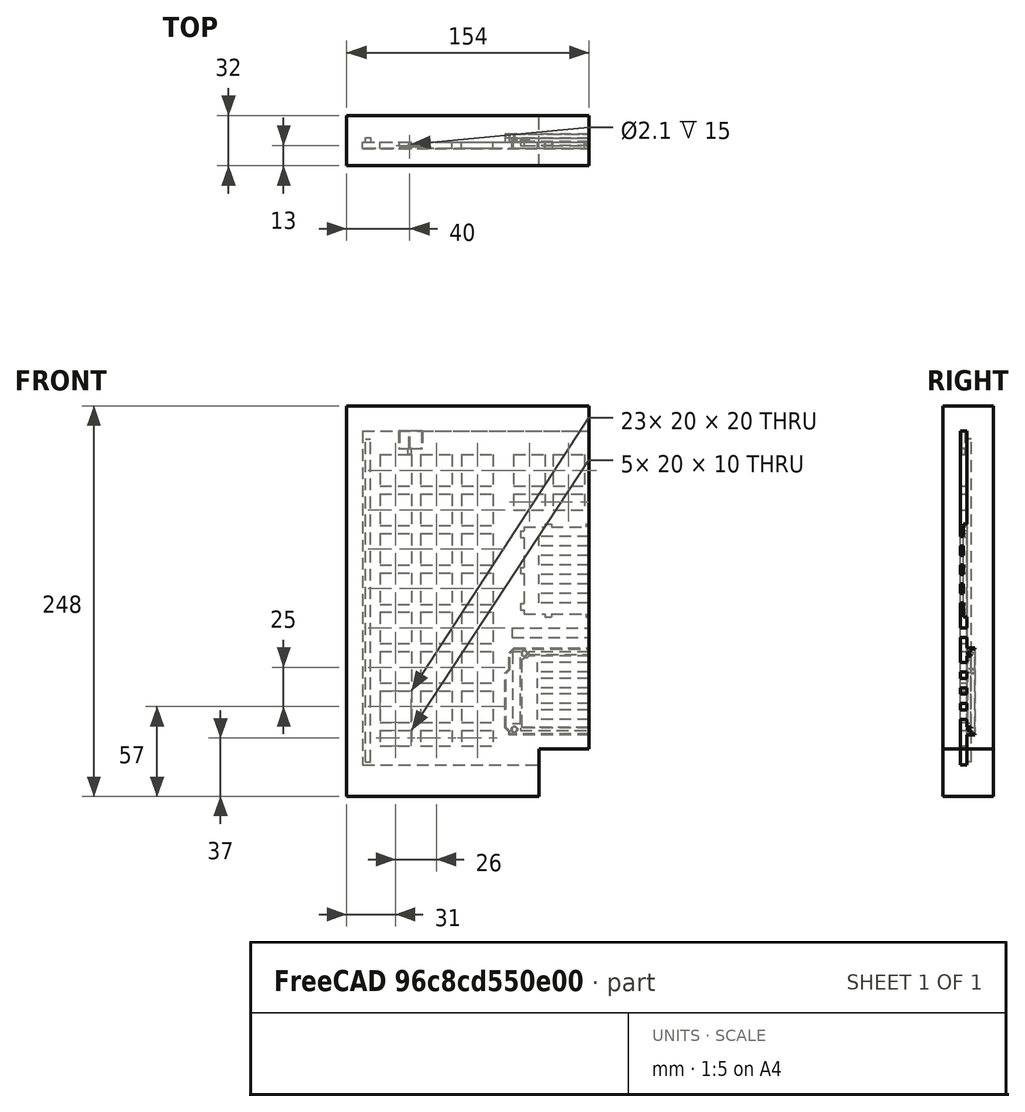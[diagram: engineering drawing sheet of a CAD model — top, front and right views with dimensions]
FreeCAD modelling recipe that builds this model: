
FCSTD DOCUMENT  (FreeCAD 0.17R13522 (Git))
Label: base_para_arduino_y_matrizia_izquierda
License: CreativeCommons Attribution-ShareAlike
LicenseURL: http://creativecommons.org/licenses/by-sa/4.0/
objects: Part::Box×18, Part::Cut×18, Part::Feature×11, Part::Fuse×9, Part::FeaturePython×6
note: 62 computed .brp shape members not serialized (recipe doc carries the construction recipe); baked Part::Feature solids carry a one-line shape summary decoded from their .brp

FEATURE [Part::Feature] Cut001001001002003001008002002034001  label="base de la base con agujeros"
  shape: bbox 280 x 4 x 200 mm, 10 faces (baked)
FEATURE [Part::Box] Box  label="fleje apoyo lateral izquierdo"
  AttacherType = Attacher::AttachEngine3D
  Height = 200
  Length = 3
  Placement = pos=(2,0,-308) rot=(0,0,1;0rad)
  Width = 3
FEATURE [Part::Feature] Box001  label="fleje apoyo lateral derecho"
  Placement = pos=(283,0,-308) rot=(0,0,1;0rad)
  shape: bbox 3 x 3 x 200 mm, 6 faces (baked)
FEATURE [Part::Box] Box002  label="Cube"
  AttacherType = Attacher::AttachEngine3D
  Height = 200
  Length = 8
  Placement = pos=(280,-4,-308) rot=(0,0,1;0rad)
  Width = 4
FEATURE [Part::Fuse] Fusion
  Base = -> Cut001001001002003001008002002034001
  Refine = true
  Tool = -> Box002
FEATURE [Part::Fuse] Fusion001
  Base = -> Box001
  Refine = true
  Tool = -> Fusion
FEATURE [Part::Fuse] Fusion002
  Base = -> Box
  Refine = true
  Tool = -> Fusion001
FEATURE [Part::Box] Box003  label="Cube001"
  AttacherType = Attacher::AttachEngine3D
  Height = 10
  Length = 10
  Placement = pos=(-2,0,-112) rot=(0,0,1;0rad)
  Width = 10
FEATURE [Part::Feature] Box003001  label="Cube002"
  Placement = pos=(280,0,-112) rot=(0,0,1;0rad)
  shape: bbox 10 x 10 x 10 mm, 6 faces (baked)
FEATURE [Part::Cut] Cut
  Base = -> Fusion002
  Refine = true
  Tool = -> Box003
FEATURE [Part::Cut] Cut001001001002003001008002002034002  label="base sin soportes y sin recorte horizontal"
  Base = -> Cut
  Refine = true
  Tool = -> Box003001
FEATURE [Part::Feature] Fusion011001  label="cortador matrizia001"
  Placement = pos=(102.5,1,-224) rot=(1,0,0;1.5708rad)
  shape: bbox 87 x 3 x 59 mm, 54 faces (baked)
FEATURE [Part::Cut] Cut001001001002003001008002002034003
  Base = -> Cut001001001002003001008002002034002
  Refine = true
  Tool = -> Fusion011001
FEATURE [Part::Box] Box003002  label="Cube003"
  AttacherType = Attacher::AttachEngine3D
  Height = 200
  Length = 288
  Placement = pos=(0,-4,-508) rot=(0,0,1;0rad)
  Width = 4
FEATURE [Part::Feature] Box003003  label="fleje apoyo lateral izquierdo001"
  Placement = pos=(2,0,-506) rot=(0,0,1;0rad)
  shape: bbox 3 x 3 x 200 mm, 6 faces (baked)
FEATURE [Part::Feature] Box001001  label="fleje apoyo lateral derecho001"
  Placement = pos=(283,0,-507) rot=(0,0,1;0rad)
  shape: bbox 3 x 3 x 200 mm, 6 faces (baked)
FEATURE [Part::Fuse] Fusion011002
  Base = -> Cut001001001002003001008002002034003
  Refine = true
  Tool = -> Box003002
FEATURE [Part::Fuse] Fusion011003
  Base = -> Box003003
  Refine = true
  Tool = -> Fusion011002
FEATURE [Part::Fuse] Fusion011004
  Base = -> Box001001
  Refine = true
  Tool = -> Fusion011003
FEATURE [Part::Feature] Arduino_MEGA_Bumper_0003001_solid001001001  label="mega_bumper002"
  Placement = pos=(193,2.5,-300) rot=(0,0.707107,0.707107;3.14159rad)
  shape: bbox 103.5 x 5.08 x 55.22 mm, 538 faces (baked)
FEATURE [Part::Fuse] Fusion011005
  Base = -> Fusion011004
  Refine = true
  Tool = -> Arduino_MEGA_Bumper_0003001_solid001001001
FEATURE [Part::Box] Box003004  label="Cube004"
  AttacherType = Attacher::AttachEngine3D
  Height = 200
  Length = 300
  Placement = pos=(-5,-6,-520) rot=(0,0,1;0rad)
  Width = 10
FEATURE [Part::Cut] Cut001001001002003001008002002034004
  Base = -> Fusion011005
  Refine = true
  Tool = -> Box003004
FEATURE [Part::Box] Box003005  label="Cube005"
  AttacherType = Attacher::AttachEngine3D
  Height = 2
  Length = 300
  Placement = pos=(0,0,-320) rot=(0,0,1;0rad)
  Width = 18
FEATURE [Part::Cut] Cut001001001002003001008002002034005
  Base = -> Cut001001001002003001008002002034004
  Refine = true
  Tool = -> Box003005
FEATURE [Part::Box] Box003006  label="Cube006"
  AttacherType = Attacher::AttachEngine3D
  Height = 20
  Length = 20
  Placement = pos=(20,0,-150) rot=(0,0,1;0rad)
  Width = 30
FEATURE [Part::FeaturePython] Array  # Draft array (typed FeaturePython)
  Angle = 360
  ArrayType = 0
  Axis = (0,0,1)
  Base = -> Box003006
  Center = (0,0,0)
  Fuse = false
  IntervalAxis = (0,0,0)
  IntervalX = (26,0,0)
  IntervalY = (0,1,0)
  IntervalZ = (0,0,-25)
  NumberPolar = 1
  NumberX = 3
  NumberY = 1
  NumberZ = 7
  Placement = pos=(-9,-17,7) rot=(0,0,1;0rad)
FEATURE [Part::Feature] Array001
  Placement = pos=(185,-17,7) rot=(0,0,1;0rad)
  shape: bbox 72 x 30 x 170 mm, 126 faces, 21 solids (baked)
FEATURE [Part::Cut] Cut001001001002003001008002002034006
  Base = -> Cut001001001002003001008002002034005
  Refine = true
  Tool = -> Array001
FEATURE [Part::Cut] Cut001001001002003001008002002034007
  Base = -> Cut001001001002003001008002002034006
  Refine = true
  Tool = -> Array
FEATURE [Part::Box] Box003007  label="Cube007"
  AttacherType = Attacher::AttachEngine3D
  Height = 20
  Length = 20
  Placement = pos=(94,0,-143) rot=(0,0,1;0rad)
  Width = 33
FEATURE [Part::FeaturePython] Array002  # Draft array (typed FeaturePython)
  Angle = 360
  ArrayType = 0
  Axis = (0,0,1)
  Base = -> Box003007
  Center = (0,0,0)
  Fuse = false
  IntervalAxis = (0,0,0)
  IntervalX = (25,0,0)
  IntervalY = (0,1,0)
  IntervalZ = (0,0,0)
  NumberPolar = 1
  NumberX = 4
  NumberY = 1
  NumberZ = 1
  Placement = pos=(2,-23,0) rot=(0,0,1;0rad)
FEATURE [Part::Box] Box003008  label="Cube008"
  AttacherType = Attacher::AttachEngine3D
  Height = 10
  Length = 20
  Placement = pos=(96,0,-158) rot=(0,0,1;0rad)
  Width = 35
FEATURE [Part::FeaturePython] Array003  # Draft array (typed FeaturePython)
  Angle = 360
  ArrayType = 0
  Axis = (0,0,1)
  Base = -> Box003008
  Center = (0,0,0)
  Fuse = false
  IntervalAxis = (0,0,0)
  IntervalX = (25,0,0)
  IntervalY = (0,1,0)
  IntervalZ = (0,0,0)
  NumberPolar = 1
  NumberX = 4
  NumberY = 1
  NumberZ = 1
  Placement = pos=(0,-24,0) rot=(0,0,1;0rad)
FEATURE [Part::Cut] Cut001001001002003001008002002034008
  Base = -> Cut001001001002003001008002002034007
  Refine = true
  Tool = -> Array002
FEATURE [Part::Cut] Cut001001001002003001008002002034009
  Base = -> Cut001001001002003001008002002034008
  Placement = pos=(194,-17,0) rot=(0,0,1;0rad)
  Refine = true
  Tool = -> Array003
FEATURE [Part::Box] Box003009  label="Cube009"
  AttacherType = Attacher::AttachEngine3D
  Height = 10
  Length = 20
  Placement = pos=(11,-4,-308) rot=(0,0,1;0rad)
  Width = 32
FEATURE [Part::FeaturePython] Array004  # Draft array (typed FeaturePython)
  Angle = 360
  ArrayType = 0
  Axis = (0,0,1)
  Base = -> Box003009
  Center = (0,0,0)
  Fuse = false
  IntervalAxis = (0,0,0)
  IntervalX = (26,0,0)
  IntervalY = (0,1,0)
  IntervalZ = (0,0,0)
  NumberPolar = 1
  NumberX = 3
  NumberY = 1
  NumberZ = 1
  Placement = pos=(388,-28,0) rot=(0,0,1;0rad)
FEATURE [Part::Feature] Array004001  label="Array005"
  Placement = pos=(194,-28,0) rot=(0,0,1;0rad)
  shape: bbox 72 x 32 x 10 mm, 18 faces, 3 solids (baked)
FEATURE [Part::Cut] Cut001001001002003001008002002034010
  Base = -> Cut001001001002003001008002002034009
  Refine = true
  Tool = -> Array004
FEATURE [Part::Box] Box003010  label="Cube010"
  AttacherType = Attacher::AttachEngine3D
  Height = 6
  Length = 63
  Placement = pos=(306,0,-185) rot=(0,0,1;0rad)
  Width = 44
FEATURE [Part::FeaturePython] Array004002  # Draft array (typed FeaturePython)
  Angle = 360
  ArrayType = 0
  Axis = (0,0,1)
  Base = -> Box003010
  Center = (0,0,0)
  Fuse = false
  IntervalAxis = (0,0,0)
  IntervalX = (1,0,0)
  IntervalY = (0,1,0)
  IntervalZ = (0,0,-12)
  NumberPolar = 1
  NumberX = 1
  NumberY = 1
  NumberZ = 4
  Placement = pos=(0,-40,4) rot=(0,0,1;0rad)
FEATURE [Part::Cut] Cut001001001002003001008002002034011
  Base = -> Cut001001001002003001008002002034010
  Refine = true
  Tool = -> Array004002
FEATURE [Part::Box] Box003011  label="Cube011"
  AttacherType = Attacher::AttachEngine3D
  Height = 6
  Length = 71
  Placement = pos=(305,0,-263) rot=(0,0,1;0rad)
  Width = 43
FEATURE [Part::FeaturePython] Array004003  # Draft array (typed FeaturePython)
  Angle = 360
  ArrayType = 0
  Axis = (0,0,1)
  Base = -> Box003011
  Center = (0,0,0)
  Fuse = false
  IntervalAxis = (0,0,0)
  IntervalX = (1,0,0)
  IntervalY = (0,1,0)
  IntervalZ = (0,0,-10)
  NumberPolar = 1
  NumberX = 1
  NumberY = 1
  NumberZ = 4
  Placement = pos=(0,-36,2) rot=(0,0,1;0rad)
FEATURE [Part::Cut] Cut001001001002003001008002002034012
  Base = -> Cut001001001002003001008002002034011
  Refine = true
  Tool = -> Array004003
FEATURE [Part::Box] Box003012  label="Cube012"
  AttacherType = Attacher::AttachEngine3D
  Height = 6
  Length = 98
  Placement = pos=(289,-30,-239) rot=(0,0,1;0rad)
  Width = 35
FEATURE [Part::Cut] Cut001001001002003001008002002034013
  Base = -> Cut001001001002003001008002002034012
  Refine = true
  Tool = -> Box003012
FEATURE [Part::Cut] Cut001001001002003001008002002034014  label="base con aireadores"
  Base = -> Cut001001001002003001008002002034013
  Refine = true
  Tool = -> Array004001
FEATURE [Part::Box] Box003013  label="cortador derecha"
  AttacherType = Attacher::AttachEngine3D
  Height = 218
  Length = 154
  Placement = pos=(184,-32,-310) rot=(0,0,1;0rad)
  Width = 32
FEATURE [Part::Feature] Box003013001  label="cortador izquierda"
  Placement = pos=(338,-32,-323) rot=(0,0,1;0rad)
  shape: bbox 154 x 32 x 218 mm, 6 faces (baked)
FEATURE [Part::Box] Box003013002  label="cortador derecha fleje"
  AttacherType = Attacher::AttachEngine3D
  Height = 30
  Length = 122
  Placement = pos=(184,-32,-340) rot=(0,0,1;0rad)
  Width = 32
FEATURE [Part::Fuse] Fusion011006  label="Fusion cortador derecho"
  Base = -> Box003013
  Refine = true
  Tool = -> Box003013002
FEATURE [Part::Box] Box003013003  label="Cube013"
  AttacherType = Attacher::AttachEngine3D
  Height = 28
  Length = 32
  Placement = pos=(306,-32,-338) rot=(0,0,1;0rad)
  Width = 32
FEATURE [Part::Fuse] Fusion011007  label="Fusion cortador izquierda"
  Base = -> Box003013001
  Refine = true
  Tool = -> Box003013003
FEATURE [Part::Cut] Cut001001001002003001008002002034015
  Base = -> Cut001001001002003001008002002034014
  Refine = true
  Tool = -> Fusion011007
FEATURE [Part::Box] Box003013004  label="Cube014"
  AttacherType = Attacher::AttachEngine3D
  Height = 10
  Length = 10
  Placement = pos=(192,-17,-113) rot=(0,0,1;0rad)
  Width = 10
FEATURE [Part::Cut] Cut001001001002003001008002002034016
  Base = -> Cut001001001002003001008002002034015
  Refine = true
  Tool = -> Box003013004
FEATURE [Part::Feature] Body001  label="cortador_parea_encastres"
  Placement = pos=(218,-19,-119) rot=(0,0,1;0rad)
  shape: bbox 15 x 2 x 20 mm, 6 faces (baked)
FEATURE [Part::Cut] Cut001001001002003001008002002034017
  Base = -> Cut001001001002003001008002002034016
  Tool = -> Body001
FEATURE [Part::Box] Box003013005  label="Cube015"
  AttacherType = Attacher::AttachEngine3D
  Height = 20
  Length = 14
  Placement = pos=(217.5,-19,-119) rot=(0,0,1;0rad)
  Width = 10
FEATURE [Part::Cut] Cut001001001002003001008002002034018  label="base izquierda"
  Base = -> Cut001001001002003001008002002034017
  Tool = -> Box003013005
